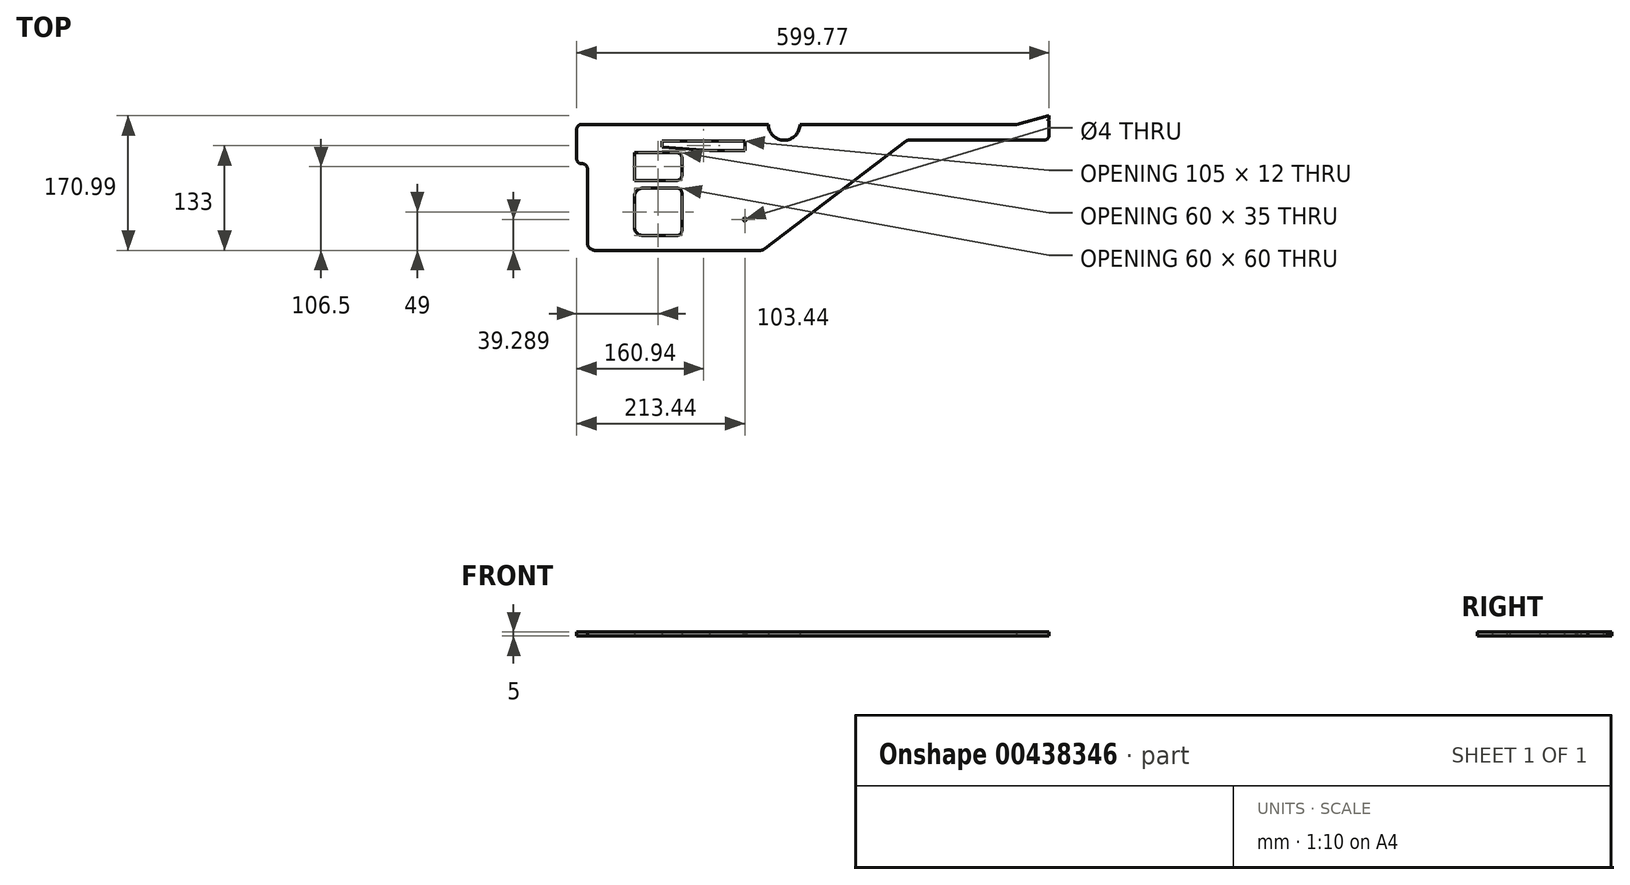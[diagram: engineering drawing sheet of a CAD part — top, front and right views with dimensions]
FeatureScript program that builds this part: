
annotation { "Feature Type Name" : "Feature", "Feature Type Description" : "" }
export const myFeature = defineFeature(function(context is Context, id is Id, definition is map)
    precondition{}
    {
        {
            var Q0;
            Q0=qCreatedBy(makeId("Top.planeOp"),FACE);
            var sketch = newSketch(context, id + "F0", { "sketchPlane" : qUnion([Q0])});
            skLineSegment(sketch, "E0", {"start": v(336.33, 4.99) * mm, "end": v(335.33, 4.99) * mm});
            skLineSegment(sketch, "E1", {"start": v(335.33, 4.99) * mm, "end": v(335.33, 5.99) * mm});
            skLineSegment(sketch, "E2", {"start": v(335.33, 5.99) * mm, "end": v(336.33, 5.99) * mm});
            skLineSegment(sketch, "E3", {"start": v(336.33, 5.99) * mm, "end": v(336.33, 10.99) * mm});
            skPoint(sketch, "E4", {"position": v(295, -0.01) * mm});
            skLineSegment(sketch, "E5", {"start": v(295, -0.01) * mm, "end": v(336.33, 10.99) * mm});
            skLineSegment(sketch, "E6", {"start": v(336.33, 4.99) * mm, "end": v(336.33, -14.01) * mm});
            skLineSegment(sketch, "E7", {"start": v(330.33, -20.01) * mm, "end": v(158.36, -20.01) * mm});
            skLineSegment(sketch, "E8", {"start": v(-24.61, -157.95) * mm, "end": v(154.72, -21.24) * mm});
            skLineSegment(sketch, "E9", {"start": v(-240, -160) * mm, "end": v(-30.67, -160) * mm});
            skPoint(sketch, "E10.visualSharp", {"position": v(-263.44, 0) * mm});
            skPoint(sketch, "E11.visualSharp", {"position": v(-27.3, -160) * mm});
            skArc(sketch, "E11.filletArc", {"start": v(-30.67, -160) * mm, "mid": v(-27.47, -159.47) * mm, "end": v(-24.61, -157.95) * mm});
            skPoint(sketch, "E12.visualSharp", {"position": v(156.33, -20.01) * mm});
            skArc(sketch, "E12.filletArc", {"start": v(158.36, -20.01) * mm, "mid": v(156.44, -20.33) * mm, "end": v(154.72, -21.24) * mm});
            skPoint(sketch, "E13.visualSharp", {"position": v(336.33, -20.01) * mm});
            skArc(sketch, "E13.filletArc", {"start": v(330.33, -20.01) * mm, "mid": v(334.57, -18.26) * mm, "end": v(336.33, -14.01) * mm});
            skPoint(sketch, "E14", {"position": v(-55, -25) * mm});
            skLineSegment(sketch, "E15", {"start": v(-50, -21) * mm, "end": v(-155, -21) * mm});
            skLineSegment(sketch, "E16", {"start": v(-50, -33) * mm, "end": v(-50, -21) * mm});
            skPoint(sketch, "E17", {"position": v(-50, -120.71) * mm});
            skCircle(sketch, "E18", {"center": v(-50, -120.71) * mm, "radius": 2 * mm});
            skPoint(sketch, "E19.visualSharp", {"position": v(-24.37, -157.07) * mm});
            skPoint(sketch, "E20", {"position": v(-130, -36) * mm});
            skLineSegment(sketch, "E21.bottom", {"start": v(-136, -36) * mm, "end": v(-190, -36) * mm});
            skLineSegment(sketch, "E21.top", {"start": v(-136, -71) * mm, "end": v(-190, -71) * mm});
            skLineSegment(sketch, "E21.left", {"start": v(-130, -42) * mm, "end": v(-130, -65) * mm});
            skLineSegment(sketch, "E21.right", {"start": v(-190, -36) * mm, "end": v(-190, -71) * mm});
            skPoint(sketch, "E22", {"position": v(-155, -25) * mm});
            skLineSegment(sketch, "E23", {"start": v(-155, -21) * mm, "end": v(-155, -25) * mm});
            skLineSegment(sketch, "E24", {"start": v(-155, -25) * mm, "end": v(-155, -29) * mm});
            skLineSegment(sketch, "E25", {"start": v(-50, -33) * mm, "end": v(-95, -33) * mm});
            skLineSegment(sketch, "E26", {"start": v(-95, -33) * mm, "end": v(-155, -29) * mm});
            skArc(sketch, "E27.filletArc", {"start": v(-257.44, 0) * mm, "mid": v(-261.69, -1.76) * mm, "end": v(-263.44, -6) * mm});
            skArc(sketch, "E28", {"start": v(-20, 0) * mm, "mid": v(0, -20) * mm, "end": v(20, 0) * mm});
            skLineSegment(sketch, "E29", {"start": v(-257.44, 0) * mm, "end": v(-20, 0) * mm});
            skLineSegment(sketch, "E30", {"start": v(20, 0) * mm, "end": v(295, -0.01) * mm});
            skPoint(sketch, "E31", {"position": v(-130, -81) * mm});
            skLineSegment(sketch, "E32.bottom", {"start": v(-136, -81) * mm, "end": v(-180, -81) * mm});
            skLineSegment(sketch, "E32.top", {"start": v(-136, -141) * mm, "end": v(-180, -141) * mm});
            skLineSegment(sketch, "E32.left", {"start": v(-130, -87) * mm, "end": v(-130, -135) * mm});
            skLineSegment(sketch, "E32.right", {"start": v(-190, -91) * mm, "end": v(-190, -131) * mm});
            skLineSegment(sketch, "E33", {"start": v(-250, -150) * mm, "end": v(-250, -56) * mm});
            skLineSegment(sketch, "E34", {"start": v(-263.44, -6) * mm, "end": v(-263.44, -44) * mm});
            skLineSegment(sketch, "E35", {"start": v(-257.44, -50) * mm, "end": v(-256, -50) * mm});
            skPoint(sketch, "E36.visualSharp", {"position": v(-250, -50) * mm});
            skArc(sketch, "E36.filletArc", {"start": v(-250, -56) * mm, "mid": v(-251.76, -51.76) * mm, "end": v(-256, -50) * mm});
            skPoint(sketch, "E37.visualSharp", {"position": v(-263.44, -50) * mm});
            skArc(sketch, "E37.filletArc", {"start": v(-263.44, -44) * mm, "mid": v(-261.69, -48.24) * mm, "end": v(-257.44, -50) * mm});
            skPoint(sketch, "E38.visualSharp", {"position": v(-250, -160) * mm});
            skArc(sketch, "E38.filletArc", {"start": v(-250, -150) * mm, "mid": v(-247.07, -157.07) * mm, "end": v(-240, -160) * mm});
            skPoint(sketch, "E39.visualSharp", {"position": v(-190, -81) * mm});
            skArc(sketch, "E39.filletArc", {"start": v(-180, -81) * mm, "mid": v(-187.07, -83.93) * mm, "end": v(-190, -91) * mm});
            skPoint(sketch, "E40.visualSharp", {"position": v(-190, -141) * mm});
            skArc(sketch, "E40.filletArc", {"start": v(-190, -131) * mm, "mid": v(-187.07, -138.07) * mm, "end": v(-180, -141) * mm});
            skPoint(sketch, "E41.visualSharp", {"position": v(-130, -141) * mm});
            skArc(sketch, "E41.filletArc", {"start": v(-136, -141) * mm, "mid": v(-131.76, -139.24) * mm, "end": v(-130, -135) * mm});
            skArc(sketch, "E42.filletArc", {"start": v(-130, -87) * mm, "mid": v(-131.76, -82.76) * mm, "end": v(-136, -81) * mm});
            skArc(sketch, "E43.filletArc", {"start": v(-130, -42) * mm, "mid": v(-131.76, -37.76) * mm, "end": v(-136, -36) * mm});
            skPoint(sketch, "E44.visualSharp", {"position": v(-130, -71) * mm});
            skArc(sketch, "E44.filletArc", {"start": v(-136, -71) * mm, "mid": v(-131.76, -69.24) * mm, "end": v(-130, -65) * mm});
            skSolve(sketch);
        }
        {
            var Q0;
            Q0 = qSketchRegion(id + "F0", true);
            extrude(context, id + "F1", {"entities" : qUnion([Q0]), "depth" : 5 * mm});
        }
    });
